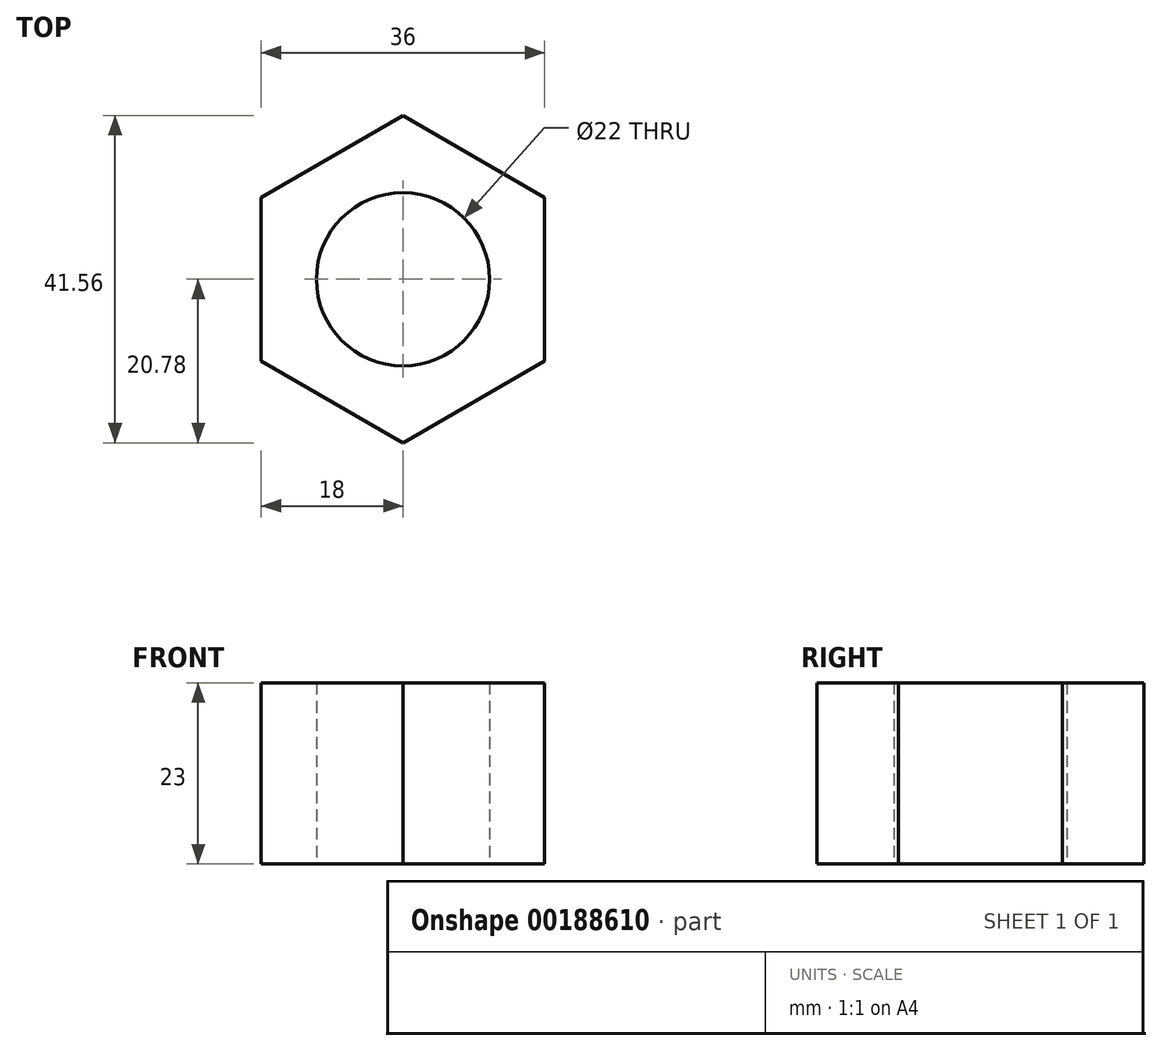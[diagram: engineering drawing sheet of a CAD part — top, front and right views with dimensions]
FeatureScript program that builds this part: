
annotation { "Feature Type Name" : "Feature", "Feature Type Description" : "" }
export const myFeature = defineFeature(function(context is Context, id is Id, definition is map)
    precondition{}
    {
        {
            var Q0;
            Q0=qCreatedBy(makeId("Top.planeOp"),FACE);
            var sketch = newSketch(context, id + "F0", { "sketchPlane" : qUnion([Q0])});
            skCircle(sketch, "E0.cCircle", {"center": v(0, 0) * mm, "radius": 20.78 * mm, "construction": true});
            skLineSegment(sketch, "E0.0", {"start": v(0, 20.78) * mm, "end": v(18, 10.4) * mm});
            skLineSegment(sketch, "E0.1", {"start": v(18, 10.4) * mm, "end": v(18, -10.4) * mm});
            skLineSegment(sketch, "E0.2", {"start": v(18, -10.4) * mm, "end": v(0, -20.78) * mm});
            skLineSegment(sketch, "E0.3", {"start": v(0, -20.78) * mm, "end": v(-18, -10.4) * mm});
            skLineSegment(sketch, "E0.4", {"start": v(-18, -10.4) * mm, "end": v(-18, 10.4) * mm});
            skLineSegment(sketch, "E0.5", {"start": v(-18, 10.4) * mm, "end": v(0, 20.78) * mm});
            skCircle(sketch, "E1", {"center": v(0, 0) * mm, "radius": 11 * mm});
            skSolve(sketch);
        }
        {
            var Q0;
            Q0 = qSketchRegion(id + "F0", true);
            extrude(context, id + "F1", {"entities" : qUnion([Q0]), "depth" : 23 * mm});
        }
    });
